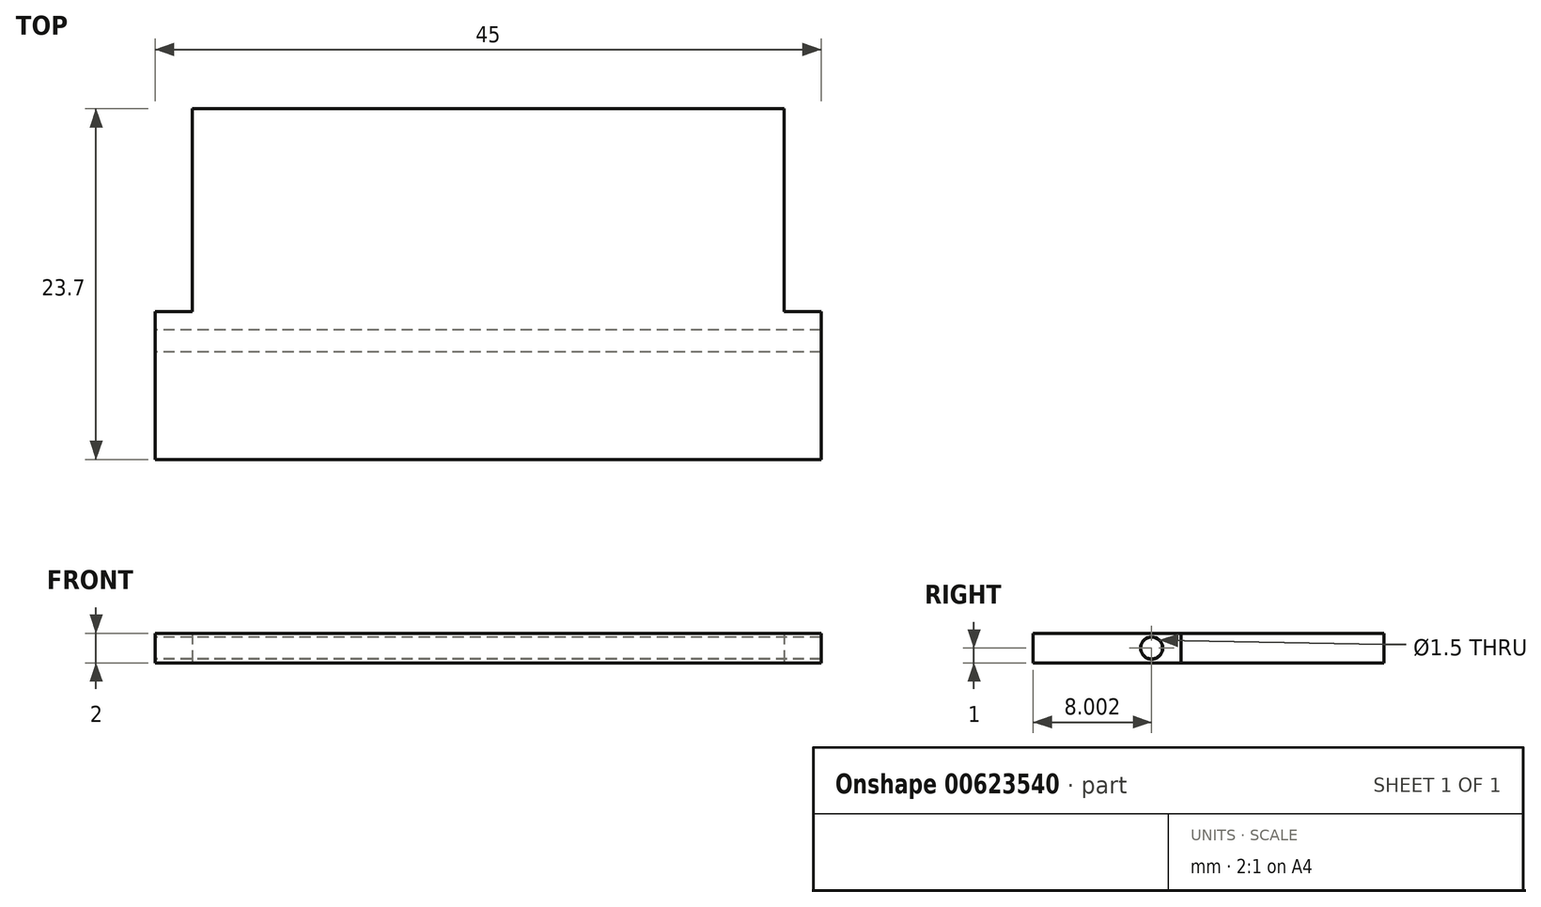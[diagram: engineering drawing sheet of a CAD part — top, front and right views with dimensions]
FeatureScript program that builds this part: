
annotation { "Feature Type Name" : "Feature", "Feature Type Description" : "" }
export const myFeature = defineFeature(function(context is Context, id is Id, definition is map)
    precondition{}
    {
        {
            var Q0;
            Q0=qCreatedBy(makeId("Top.planeOp"),FACE);
            var sketch = newSketch(context, id + "F0", { "sketchPlane" : qUnion([Q0])});
            skLineSegment(sketch, "E0.bottom", {"start": v(20, -8.85) * mm, "end": v(-20, -8.85) * mm});
            skLineSegment(sketch, "E0.top", {"start": v(20, 8.85) * mm, "end": v(-20, 8.85) * mm});
            skLineSegment(sketch, "E0.left", {"start": v(20, -8.85) * mm, "end": v(20, 8.85) * mm});
            skLineSegment(sketch, "E0.right", {"start": v(-20, -8.85) * mm, "end": v(-20, 8.85) * mm});
            skPoint(sketch, "E0.middle", {"position": v(0, 0) * mm});
            skSolve(sketch);
        }
        {
            var Q0;
            Q0 = qSketchRegion(id + "F0", true);
            extrude(context, id + "F1", {"entities" : qUnion([Q0]), "depth" : 2 * mm, "offsetDistance" : 25.4 * mm});
        }
        {
            var Q0;
            Q0=makeQuery(id+"F1.opExtrude","SWEPT_FACE",FACE,{"disambiguationData":[OSD([sQuery(id+"F0.wireOp",EDGE,"E0.bottom")])]});
            var sketch = newSketch(context, id + "F2", { "sketchPlane" : qUnion([Q0])});
            skLineSegment(sketch, "E1.bottom", {"start": v(-20, 0) * mm, "end": v(-22.5, 0) * mm});
            skLineSegment(sketch, "E1.top", {"start": v(-20, 2) * mm, "end": v(-22.5, 2) * mm});
            skLineSegment(sketch, "E1.right", {"start": v(-22.5, 0) * mm, "end": v(-22.5, 2) * mm});
            skPoint(sketch, "E1.middle", {"position": v(-20, 1) * mm});
            skLineSegment(sketch, "E2.bottom", {"start": v(22.5, 0) * mm, "end": v(20, 0) * mm});
            skLineSegment(sketch, "E2.top", {"start": v(22.5, 2) * mm, "end": v(20, 2) * mm});
            skLineSegment(sketch, "E2.left", {"start": v(22.5, 0) * mm, "end": v(22.5, 2) * mm});
            skPoint(sketch, "E2.middle", {"position": v(20, 1) * mm});
            skLineSegment(sketch, "E3", {"start": v(-20, 2) * mm, "end": v(-20, 0) * mm});
            skLineSegment(sketch, "E4", {"start": v(20, 2) * mm, "end": v(20, 0) * mm});
            skPoint(sketch, "E5.orphan", {"position": v(-17.5, 2) * mm});
            skPoint(sketch, "E6.orphan", {"position": v(-17.5, 0) * mm});
            skPoint(sketch, "E2.right.end.orphan", {"position": v(17.5, 2) * mm});
            skPoint(sketch, "E7.orphan", {"position": v(17.5, 0) * mm});
            skSolve(sketch);
        }
        {
            var Q0;
            Q0=makeQuery(id+"F2.imprint","IMPRINT",FACE,{"disambiguationData":[TD([[makeQuery(id+"F2.imprint","IMPRINT",EDGE,{"derivedFrom":sQuery(id+"F2.wireOp",EDGE,"E3")}),1.0]])]});
            cPlane(context, id + "F3", {"entities" : qUnion([Q0]), "cplaneType" : CPlaneType.OFFSET, "offset" : 0 * mm, "width" : 152.4 * mm, "height" : 152.4 * mm});
        }
        {
            var Q0;
            Q0=qCreatedBy(id+"F3.planeOp",FACE);
            var sketch = newSketch(context, id + "F4", { "sketchPlane" : qUnion([Q0])});
            skLineSegment(sketch, "E8.bottom", {"start": v(-22.5, 2) * mm, "end": v(22.5, 2) * mm});
            skLineSegment(sketch, "E8.top", {"start": v(-22.5, 0) * mm, "end": v(22.5, 0) * mm});
            skLineSegment(sketch, "E8.left", {"start": v(-22.5, 2) * mm, "end": v(-22.5, 0) * mm});
            skLineSegment(sketch, "E8.right", {"start": v(22.5, 2) * mm, "end": v(22.5, 0) * mm});
            skSolve(sketch);
        }
        {
            var Q0;
            Q0 = qSketchRegion(id + "F4", true);
            extrude(context, id + "F5", {"entities" : qUnion([Q0]), "depth" : 6 * mm, "offsetDistance" : 25.4 * mm});
        }
        {
            var Q0;
            Q0 = qSketchRegion(id + "F2", true);
            extrude(context, id + "F6", {"entities" : qUnion([Q0]), "operationType" : NewBodyOperationType.ADD, "oppositeDirection" : true, "depth" : 4 * mm, "offsetDistance" : 25.4 * mm});
        }
        {
            var Q0;
            Q0=makeQuery(id+"F6.opExtrude","SWEPT_FACE",FACE,{"disambiguationData":[OSD([sQuery(id+"F2.wireOp",EDGE,"E1.right")])]});
            var sketch = newSketch(context, id + "F7", { "sketchPlane" : qUnion([Q0])});
            skCircle(sketch, "E9", {"center": v(6.85, 1) * mm, "radius": 0.75 * mm});
            skSolve(sketch);
        }
        {
            var Q0;
            Q0 = qSketchRegion(id + "F7", true);
            extrude(context, id + "F8", {"entities" : qUnion([Q0]), "operationType" : NewBodyOperationType.REMOVE, "oppositeDirection" : true, "depth" : 45 * mm, "offsetDistance" : 25.4 * mm});
        }
        {
            var Q0;
            Q0=makeQuery(id+"F1.opExtrude","SWEPT_FACE",FACE,{"disambiguationData":[OSD([sQuery(id+"F0.wireOp",EDGE,"E0.right")])]});
            var sketch = newSketch(context, id + "F9", { "sketchPlane" : qUnion([Q0])});
            skCircle(sketch, "E10", {"center": v(6.85, 1) * mm, "radius": 0.75 * mm});
            skSolve(sketch);
        }
        {
            var Q0;
            Q0 = qSketchRegion(id + "F9", true);
            extrude(context, id + "F10", {"entities" : qUnion([Q0]), "operationType" : NewBodyOperationType.REMOVE, "oppositeDirection" : true, "depth" : 40 * mm, "offsetDistance" : 25.4 * mm});
        }
        {
            var Q0;
            Q0=makeQuery(id+"F6.opExtrude","SWEPT_FACE",FACE,{"disambiguationData":[OSD([sQuery(id+"F2.wireOp",EDGE,"E1.right")])]});
            var sketch = newSketch(context, id + "F11", { "sketchPlane" : qUnion([Q0])});
            skPoint(sketch, "E11.orphan", {"position": v(4.85, 2) * mm});
            skPoint(sketch, "E12.end.orphan", {"position": v(8.85, 0) * mm});
            skCircle(sketch, "E13", {"center": v(6.85, 1) * mm, "radius": 0.73 * mm});
            skSolve(sketch);
        }
        {
            var Q0;
            Q0 = qSketchRegion(id + "F11", true);
            extrude(context, id + "F12", {"entities" : qUnion([Q0]), "oppositeDirection" : true, "depth" : 45 * mm, "offsetDistance" : 25.4 * mm});
        }
    });
